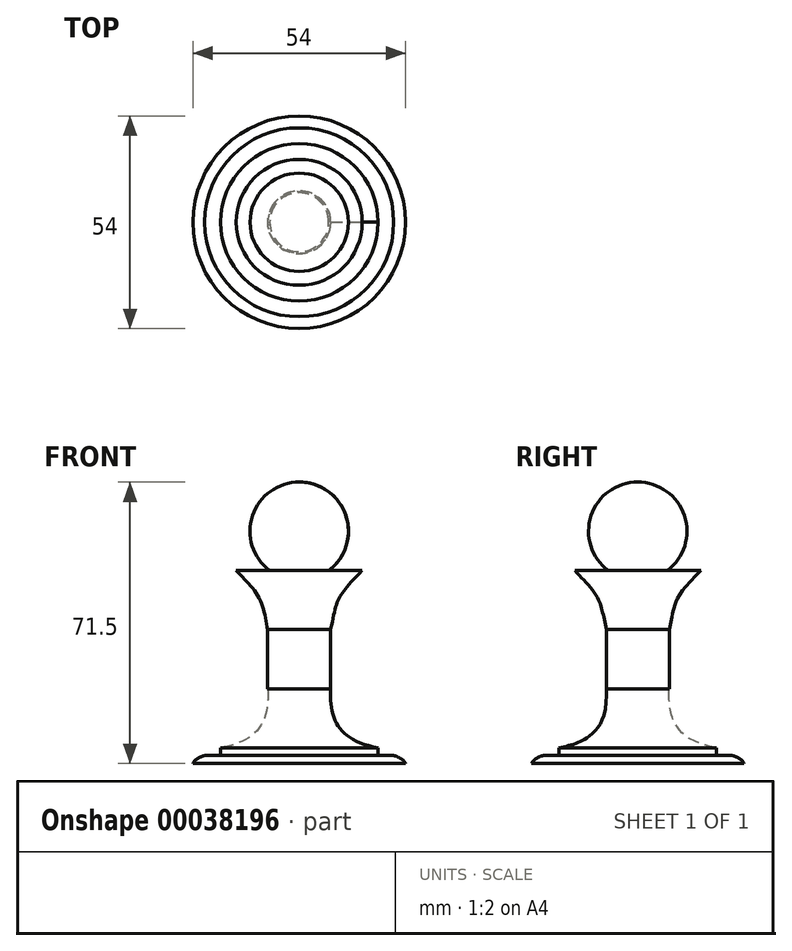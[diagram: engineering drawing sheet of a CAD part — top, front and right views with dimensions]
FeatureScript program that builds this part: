
annotation { "Feature Type Name" : "Feature", "Feature Type Description" : "" }
export const myFeature = defineFeature(function(context is Context, id is Id, definition is map)
    precondition{}
    {
        {
            var Q0;
            Q0=qCreatedBy(makeId("Front.planeOp"),FACE);
            var sketch = newSketch(context, id + "F0", { "sketchPlane" : qUnion([Q0])});
            skArc(sketch, "E0", {"start": v(7.5, 6.64) * mm, "mid": v(11.86, 20.6) * mm, "end": v(0, 29.14) * mm});
            skLineSegment(sketch, "E1", {"start": v(0, 16.64) * mm, "end": v(0, 6.64) * mm});
            skLineSegment(sketch, "E2", {"start": v(7.5, 6.64) * mm, "end": v(16, 6.64) * mm});
            skLineSegment(sketch, "E3", {"start": v(0, 6.64) * mm, "end": v(0, -8.36) * mm});
            skLineSegment(sketch, "E4", {"start": v(8, -8.36) * mm, "end": v(8, -23.36) * mm});
            skLineSegment(sketch, "E5", {"start": v(0, -23.36) * mm, "end": v(0, -38.36) * mm});
            skLineSegment(sketch, "E6", {"start": v(0, -38.36) * mm, "end": v(0, -40.36) * mm});
            skLineSegment(sketch, "E7", {"start": v(20, -40.36) * mm, "end": v(24, -40.36) * mm});
            skLineSegment(sketch, "E8", {"start": v(0, -40.36) * mm, "end": v(0, -42.36) * mm});
            skLineSegment(sketch, "E9", {"start": v(0, -42.36) * mm, "end": v(27, -42.36) * mm});
            skFitSpline(sketch, "E10", {"points": [v(16, 6.64) * mm, v(8, -8.36) * mm], "startDerivative": vector(-19.1, -19.93) * mm, "endDerivative": vector(-4.9, -25.07) * mm});
            skLineSegment(sketch, "E11", {"start": v(20, -38.36) * mm, "end": v(20, -40.36) * mm});
            skFitSpline(sketch, "E12", {"points": [v(8, -23.36) * mm, v(20, -38.36) * mm], "startDerivative": vector(-1.27, -23.72) * mm, "endDerivative": vector(30, -5.2) * mm});
            skFitSpline(sketch, "E13", {"points": [v(24, -40.36) * mm, v(27, -42.36) * mm], "startDerivative": vector(5.35, -1.47) * mm, "endDerivative": vector(0.97, -2.15) * mm});
            skLineSegment(sketch, "E14", {"start": v(0, 29.14) * mm, "end": v(0, 16.64) * mm});
            skLineSegment(sketch, "E15", {"start": v(0, -8.36) * mm, "end": v(0, -23.36) * mm});
            skSolve(sketch);
        }
        {
            var Q0;
            Q0=makeQuery(id+"F0.imprint","IMPRINT",FACE,{"disambiguationData":[TD([[makeQuery(id+"F0.imprint","IMPRINT",EDGE,{"derivedFrom":sQuery(id+"F0.wireOp",EDGE,"E0")}),1.0]])]});
            var Q1;
            Q1=sQuery(id+"F0.wireOp",EDGE,"E14");
            revolve(context, id + "F1", {"entities" : qUnion([Q0]), "axis" : qUnion([Q1]), "revolveType" : RevolveType.FULL});
        }
    });
